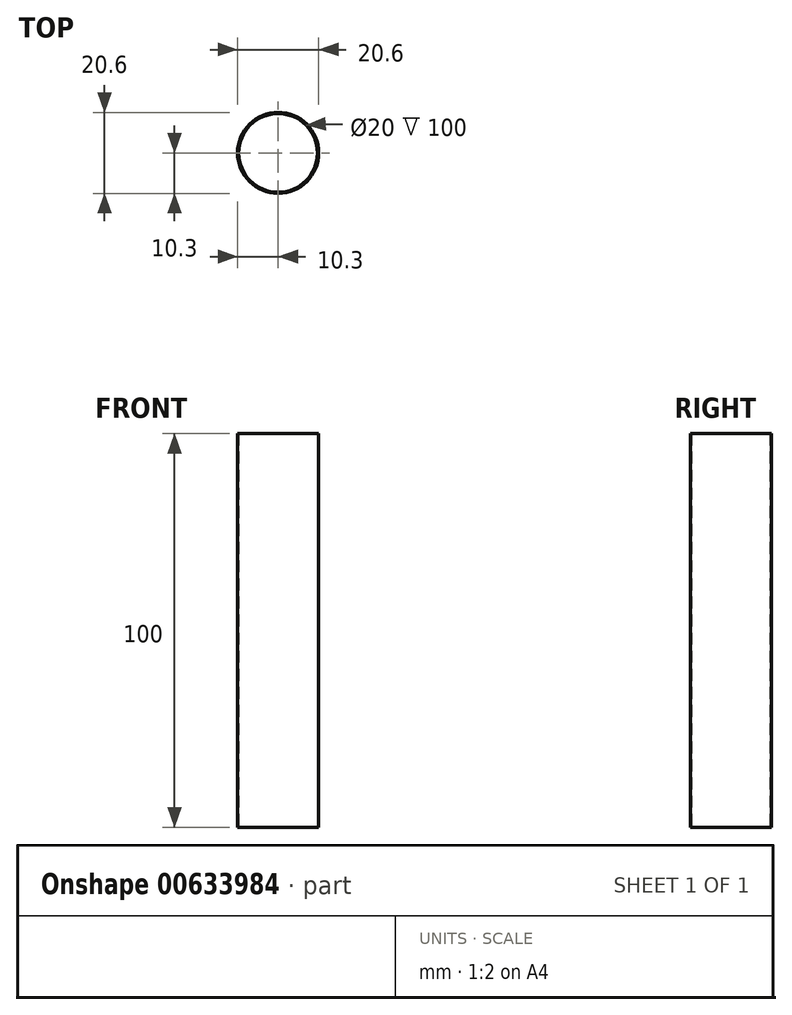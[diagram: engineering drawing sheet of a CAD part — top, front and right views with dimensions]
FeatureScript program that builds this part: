
annotation { "Feature Type Name" : "Feature", "Feature Type Description" : "" }
export const myFeature = defineFeature(function(context is Context, id is Id, definition is map)
    precondition{}
    {
        {
            var Q0;
            Q0=qCreatedBy(makeId("Top.planeOp"),FACE);
            var sketch = newSketch(context, id + "F0", { "sketchPlane" : qUnion([Q0])});
            skCircle(sketch, "E0", {"center": v(0, 0) * mm, "radius": 10 * mm});
            skCircle(sketch, "E1", {"center": v(0, 0) * mm, "radius": 10.3 * mm});
            skSolve(sketch);
        }
        {
            var Q0;
            Q0 = qSketchRegion(id + "F0", true);
            extrude(context, id + "F1", {"entities" : qUnion([Q0]), "depth" : 100 * mm, "offsetDistance" : 25 * mm});
        }
    });
